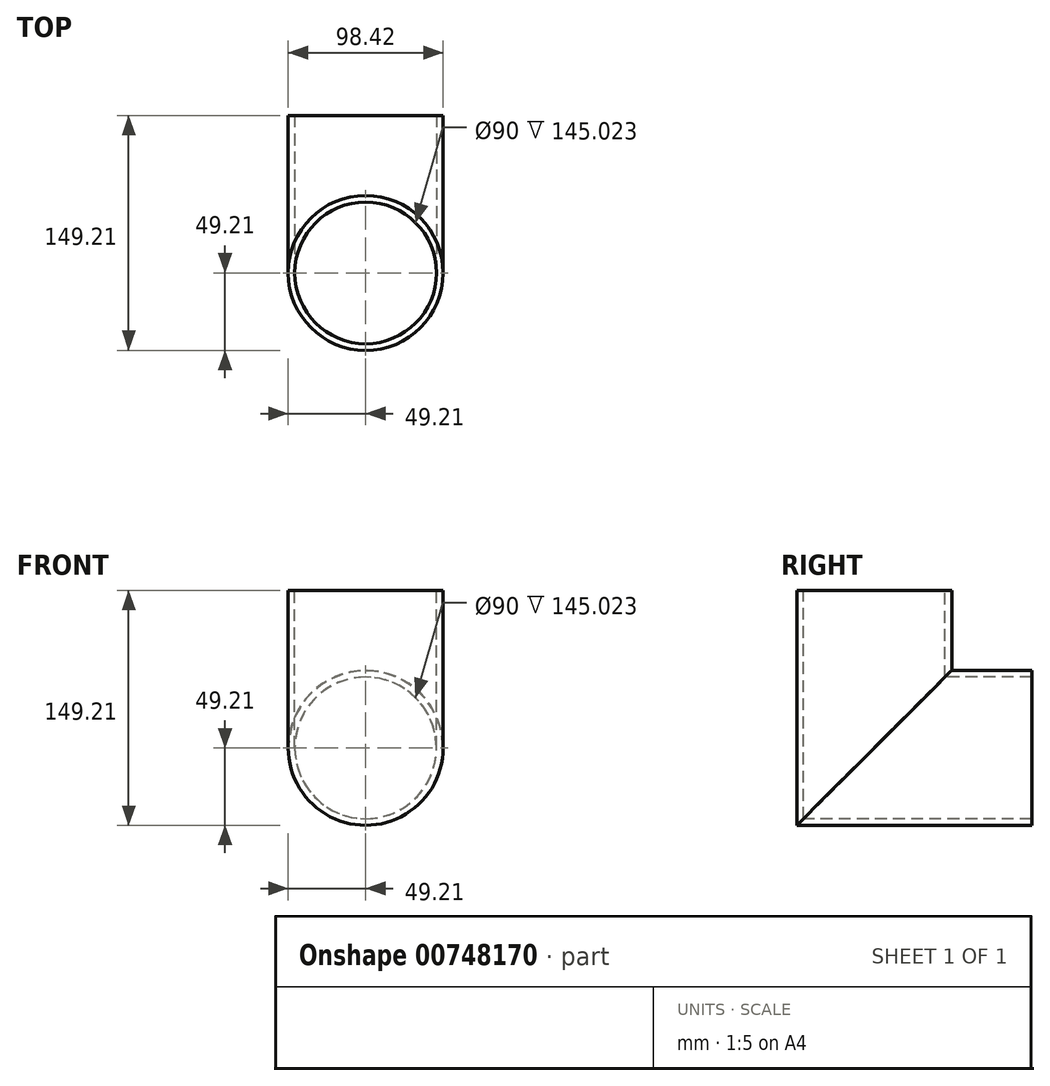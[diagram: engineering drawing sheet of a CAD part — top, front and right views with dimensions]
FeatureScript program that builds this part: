
annotation { "Feature Type Name" : "Feature", "Feature Type Description" : "" }
export const myFeature = defineFeature(function(context is Context, id is Id, definition is map)
    precondition{}
    {
        {
            var Q0;
            Q0=qCreatedBy(makeId("Front.planeOp"),FACE);
            var sketch = newSketch(context, id + "F0", { "sketchPlane" : qUnion([Q0])});
            skCircle(sketch, "E0", {"center": v(0, 0) * mm, "radius": 49.21 * mm});
            skSolve(sketch);
        }
        {
            var Q0;
            Q0=qCreatedBy(makeId("Right.planeOp"),FACE);
            var sketch = newSketch(context, id + "F1", { "sketchPlane" : qUnion([Q0])});
            skLineSegment(sketch, "E1", {"start": v(0, 0) * mm, "end": v(-100, 0) * mm});
            skLineSegment(sketch, "E2", {"start": v(-100, 0) * mm, "end": v(-100, 100) * mm});
            skSolve(sketch);
        }
        {
            var Q0;
            Q0=makeQuery(id+"F0.imprint","IMPRINT",FACE,{"disambiguationData":[TD([[makeQuery(id+"F0.imprint","IMPRINT",EDGE,{"derivedFrom":sQuery(id+"F0.wireOp",EDGE,"E0")}),1.0]])]});
            var Q1;
            Q1=sQuery(id+"F1.wireOp",EDGE,"E1");
            var Q2;
            Q2=sQuery(id+"F1.wireOp",EDGE,"E2");
            sweep(context, id + "F2", {"profiles" : qUnion([Q0]), "path" : qUnion([Q1, Q2])});
        }
        {
            var Q0;
            Q0=makeQuery(id+"F2.opSweep","CAP_FACE",FACE,{"disambiguationData":[OSD([sQuery(id+"F0.wireOp",EDGE,"E0"),sQuery(id+"F1.wireOp",VERTEX,"E1.start")])],"isStart":true});
            var sketch = newSketch(context, id + "F3", { "sketchPlane" : qUnion([Q0])});
            skCircle(sketch, "E3", {"center": v(0, 0) * mm, "radius": 45 * mm});
            skSolve(sketch);
        }
        {
            var Q0;
            Q0=qCreatedBy(makeId("Right.planeOp"),FACE);
            var sketch = newSketch(context, id + "F4", { "sketchPlane" : qUnion([Q0])});
            skLineSegment(sketch, "E4", {"start": v(0, 0) * mm, "end": v(-100, 0) * mm});
            skLineSegment(sketch, "E5", {"start": v(-100, 0) * mm, "end": v(-100, 100) * mm});
            skSolve(sketch);
        }
        {
            var Q0;
            Q0=makeQuery(id+"F3.imprint","IMPRINT",FACE,{"disambiguationData":[TD([[makeQuery(id+"F3.imprint","IMPRINT",EDGE,{"derivedFrom":sQuery(id+"F3.wireOp",EDGE,"E3")}),1.0]])]});
            var Q1;
            Q1=sQuery(id+"F4.wireOp",EDGE,"E4");
            var Q2;
            Q2=sQuery(id+"F4.wireOp",EDGE,"E5");
            sweep(context, id + "F5", {"operationType" : NewBodyOperationType.REMOVE, "profiles" : qUnion([Q0]), "path" : qUnion([Q1, Q2])});
        }
    });
